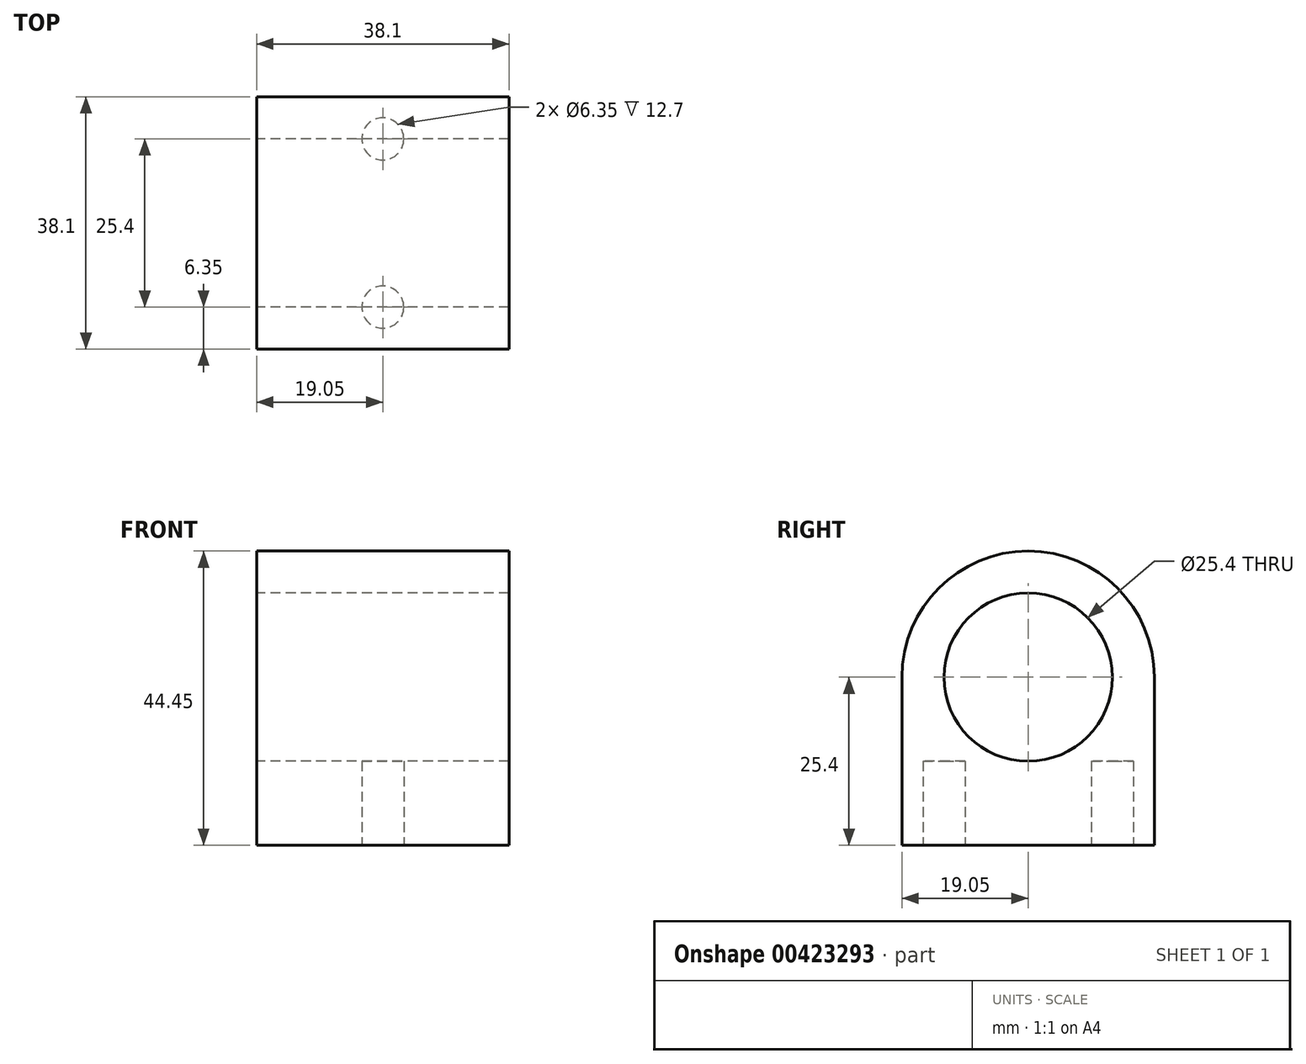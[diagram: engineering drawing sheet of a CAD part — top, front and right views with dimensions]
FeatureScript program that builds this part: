
annotation { "Feature Type Name" : "Feature", "Feature Type Description" : "" }
export const myFeature = defineFeature(function(context is Context, id is Id, definition is map)
    precondition{}
    {
        {
            var Q0;
            Q0=qCreatedBy(makeId("Right.planeOp"),FACE);
            var sketch = newSketch(context, id + "F0", { "sketchPlane" : qUnion([Q0])});
            skCircle(sketch, "E0", {"center": v(0, 0) * mm, "radius": 12.7 * mm});
            skCircle(sketch, "E1", {"center": v(0, 0) * mm, "radius": 19.05 * mm});
            skLineSegment(sketch, "E2.bottom", {"start": v(-19.05, 0) * mm, "end": v(19.05, 0) * mm});
            skLineSegment(sketch, "E2.top", {"start": v(-19.05, -25.4) * mm, "end": v(19.05, -25.4) * mm});
            skLineSegment(sketch, "E2.left", {"start": v(-19.05, 0) * mm, "end": v(-19.05, -25.4) * mm});
            skLineSegment(sketch, "E2.right", {"start": v(19.05, 0) * mm, "end": v(19.05, -25.4) * mm});
            skSolve(sketch);
        }
        {
            var Q0;
            Q0 = qSketchRegion(id + "F0", true);
            extrude(context, id + "F1", {"entities" : qUnion([Q0]), "endBound" : BoundingType.SYMMETRIC, "depth" : 38.1 * mm});
        }
        {
            var Q0;
            Q0=makeQuery(id+"F1.opExtrude","SWEPT_FACE",FACE,{"disambiguationData":[OSD([sQuery(id+"F0.wireOp",EDGE,"E2.top")])]});
            var sketch = newSketch(context, id + "F2", { "sketchPlane" : qUnion([Q0])});
            skCircle(sketch, "E3", {"center": v(0, 12.7) * mm, "radius": 3.18 * mm});
            skCircle(sketch, "E4", {"center": v(0, -12.7) * mm, "radius": 3.18 * mm});
            skSolve(sketch);
        }
        {
            var Q0;
            Q0=makeQuery(id+"F2.imprint","IMPRINT",FACE,{"disambiguationData":[TD([[makeQuery(id+"F2.imprint","IMPRINT",EDGE,{"derivedFrom":sQuery(id+"F2.wireOp",EDGE,"E3")}),1.0]])]});
            var Q1;
            Q1=makeQuery(id+"F2.imprint","IMPRINT",FACE,{"disambiguationData":[TD([[makeQuery(id+"F2.imprint","IMPRINT",EDGE,{"derivedFrom":sQuery(id+"F2.wireOp",EDGE,"E4")}),1.0]])]});
            extrude(context, id + "F3", {"entities" : qUnion([Q0, Q1]), "operationType" : NewBodyOperationType.REMOVE, "oppositeDirection" : true, "depth" : 12.7 * mm});
        }
    });
